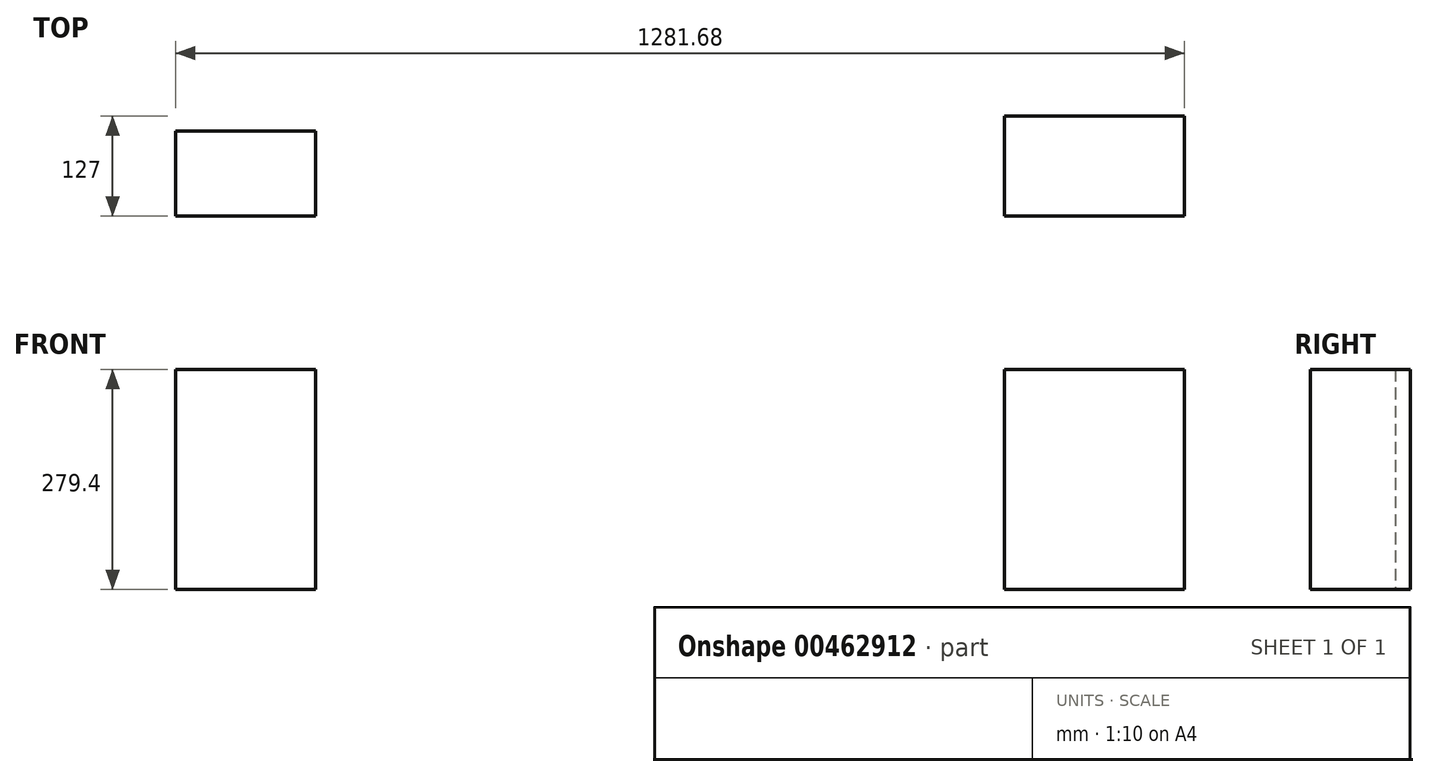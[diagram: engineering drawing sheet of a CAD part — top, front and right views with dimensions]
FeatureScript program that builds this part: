
annotation { "Feature Type Name" : "Feature", "Feature Type Description" : "" }
export const myFeature = defineFeature(function(context is Context, id is Id, definition is map)
    precondition{}
    {
        {
            var Q0;
            Q0=qCreatedBy(makeId("Top.planeOp"),FACE);
            var sketch = newSketch(context, id + "F0", { "sketchPlane" : qUnion([Q0])});
            skLineSegment(sketch, "E0.bottom", {"start": v(0, 0) * mm, "end": v(279.4, 0) * mm});
            skLineSegment(sketch, "E0.top", {"start": v(0, 355.6) * mm, "end": v(279.4, 355.6) * mm});
            skLineSegment(sketch, "E0.left", {"start": v(0, 0) * mm, "end": v(0, 355.6) * mm});
            skLineSegment(sketch, "E0.right", {"start": v(279.4, 0) * mm, "end": v(279.4, 177.8) * mm});
            skLineSegment(sketch, "E1", {"start": v(0, 177.8) * mm, "end": v(279.4, 177.8) * mm});
            skLineSegment(sketch, "E2.bottom", {"start": v(471.64, 0) * mm, "end": v(751.04, 0) * mm});
            skLineSegment(sketch, "E2.top", {"start": v(471.64, 355.6) * mm, "end": v(751.04, 355.6) * mm});
            skLineSegment(sketch, "E2.left", {"start": v(471.64, 0) * mm, "end": v(471.64, 355.6) * mm});
            skLineSegment(sketch, "E2.right", {"start": v(751.04, 0) * mm, "end": v(751.04, 107.95) * mm});
            skLineSegment(sketch, "E3", {"start": v(471.64, 107.95) * mm, "end": v(751.04, 107.95) * mm});
            skLineSegment(sketch, "E4", {"start": v(471.64, 215.9) * mm, "end": v(751.04, 215.9) * mm});
            skLineSegment(sketch, "E5", {"start": v(751.04, 215.9) * mm, "end": v(751.04, 355.6) * mm});
            skLineSegment(sketch, "E6", {"start": v(751.04, 107.95) * mm, "end": v(751.04, 215.9) * mm});
            skLineSegment(sketch, "E7.bottom", {"start": v(1053.08, 0) * mm, "end": v(1332.48, 0) * mm});
            skLineSegment(sketch, "E7.top", {"start": v(1053.08, 355.6) * mm, "end": v(1332.48, 355.6) * mm});
            skLineSegment(sketch, "E7.left", {"start": v(1053.08, 0) * mm, "end": v(1053.08, 355.6) * mm});
            skLineSegment(sketch, "E7.right", {"start": v(1332.48, 0) * mm, "end": v(1332.48, 127) * mm});
            skLineSegment(sketch, "E8", {"start": v(1053.08, 127) * mm, "end": v(1332.48, 127) * mm});
            skLineSegment(sketch, "E9.bottom", {"start": v(1515.24, 0) * mm, "end": v(1794.64, 0) * mm});
            skLineSegment(sketch, "E9.top", {"start": v(1515.24, 355.6) * mm, "end": v(1794.64, 355.6) * mm});
            skLineSegment(sketch, "E9.left", {"start": v(1515.24, 0) * mm, "end": v(1515.24, 355.6) * mm});
            skLineSegment(sketch, "E9.right", {"start": v(1794.64, 0) * mm, "end": v(1794.64, 101.6) * mm});
            skLineSegment(sketch, "E10", {"start": v(1515.24, 101.6) * mm, "end": v(1794.64, 101.6) * mm});
            skLineSegment(sketch, "E11", {"start": v(1515.24, 203.2) * mm, "end": v(1794.64, 203.2) * mm});
            skLineSegment(sketch, "E12", {"start": v(1794.64, 203.2) * mm, "end": v(1794.64, 355.6) * mm});
            skLineSegment(sketch, "E13", {"start": v(1794.64, 101.6) * mm, "end": v(1794.64, 203.2) * mm});
            skLineSegment(sketch, "E14.bottom", {"start": v(0, 626.35) * mm, "end": v(177.8, 626.35) * mm});
            skLineSegment(sketch, "E14.top", {"start": v(0, 518.4) * mm, "end": v(177.8, 518.4) * mm});
            skLineSegment(sketch, "E14.left", {"start": v(0, 626.35) * mm, "end": v(0, 518.4) * mm});
            skLineSegment(sketch, "E14.right", {"start": v(177.8, 626.35) * mm, "end": v(177.8, 518.4) * mm});
            skLineSegment(sketch, "E15.bottom", {"start": v(1053.08, 645.4) * mm, "end": v(1281.68, 645.4) * mm});
            skLineSegment(sketch, "E15.top", {"start": v(1053.08, 518.4) * mm, "end": v(1281.68, 518.4) * mm});
            skLineSegment(sketch, "E15.left", {"start": v(1053.08, 645.4) * mm, "end": v(1053.08, 518.4) * mm});
            skLineSegment(sketch, "E15.right", {"start": v(1281.68, 645.4) * mm, "end": v(1281.68, 518.4) * mm});
            skLineSegment(sketch, "E16", {"start": v(279.4, 177.8) * mm, "end": v(279.4, 355.6) * mm});
            skLineSegment(sketch, "E17", {"start": v(1332.48, 127) * mm, "end": v(1332.48, 355.6) * mm});
            skSolve(sketch);
        }
        {
            var Q0;
            Q0=makeQuery(id+"F0.imprint","IMPRINT",FACE,{"disambiguationData":[TD([[makeQuery(id+"F0.imprint","IMPRINT",EDGE,{"derivedFrom":sQuery(id+"F0.wireOp",EDGE,"E14.bottom")}),-1.0]])]});
            var Q1;
            Q1=makeQuery(id+"F0.imprint","IMPRINT",FACE,{"disambiguationData":[TD([[makeQuery(id+"F0.imprint","IMPRINT",EDGE,{"derivedFrom":sQuery(id+"F0.wireOp",EDGE,"E15.bottom")}),-1.0]])]});
            extrude(context, id + "F1", {"entities" : qUnion([Q0, Q1]), "depth" : 279.4 * mm, "offsetDistance" : 25.4 * mm});
        }
    });
